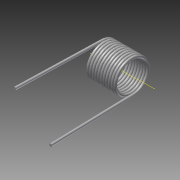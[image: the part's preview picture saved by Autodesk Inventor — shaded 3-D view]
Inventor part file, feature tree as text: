
AUTODESK INVENTOR PART (.ipt)
format: ipt  version: 2014 (Build 180170000, 170)  size: 452,608 bytes
history: native  units: in
note: dims shown in document units (in); Inventor stores cm internally (conversion verified against a paired STEP export)
features: other x3, plane x1, sketch x1, imported_body x1
ambient origin geometry x8: Origin, YZ Plane, XZ Plane, XY Plane, X Axis, Y Axis, Z Axis, Center Point
bodies: Body1 (feature_tree)
feature tree (6):
  parser-record x1  (decoder bookkeeping rows leaked as tree rows — omitted from the tree; the rows remain in map.json)
  other  "9271K1341"
  plane  "Work Plane1"
  sketch  "Sketch1"
  other  "Work Axis1"
  imported_body  "Base1"
